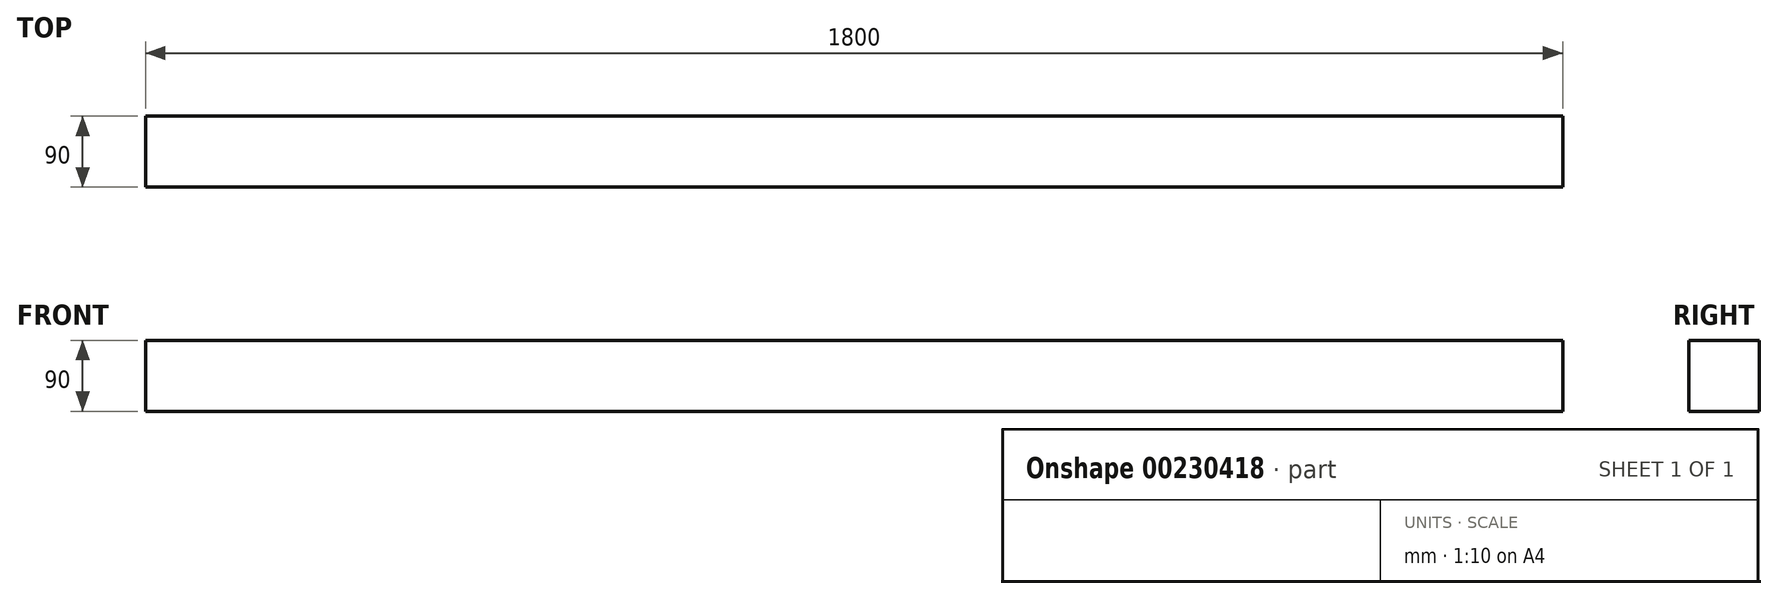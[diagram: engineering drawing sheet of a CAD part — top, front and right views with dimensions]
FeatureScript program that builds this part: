
annotation { "Feature Type Name" : "Feature", "Feature Type Description" : "" }
export const myFeature = defineFeature(function(context is Context, id is Id, definition is map)
    precondition{}
    {
        {
            var Q0;
            Q0=qCreatedBy(makeId("Right.planeOp"),FACE);
            var sketch = newSketch(context, id + "F0", { "sketchPlane" : qUnion([Q0])});
            skLineSegment(sketch, "E0.bottom", {"start": v(-44.54, 52.17) * mm, "end": v(45.46, 52.17) * mm});
            skLineSegment(sketch, "E0.top", {"start": v(-44.54, -37.83) * mm, "end": v(45.46, -37.83) * mm});
            skLineSegment(sketch, "E0.left", {"start": v(-44.54, 52.17) * mm, "end": v(-44.54, -37.83) * mm});
            skLineSegment(sketch, "E0.right", {"start": v(45.46, 52.17) * mm, "end": v(45.46, -37.83) * mm});
            skSolve(sketch);
        }
        {
            var Q0;
            Q0 = qSketchRegion(id + "F0", true);
            extrude(context, id + "F1", {"entities" : qUnion([Q0]), "oppositeDirection" : true, "depth" : 1800 * mm});
        }
    });
